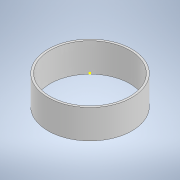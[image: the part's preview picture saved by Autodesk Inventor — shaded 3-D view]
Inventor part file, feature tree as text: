
AUTODESK INVENTOR PART (.ipt)
format: ipt  version: 2020 (Build 240168000, 168)  size: 233,472 bytes
history: native  units: in
note: dims shown in document units (in); Inventor stores cm internally (conversion verified against a paired STEP export)
features: sketch x2, extrude x1
ambient origin geometry x8: Origin, YZ Plane, XZ Plane, XY Plane, X Axis, Y Axis, Z Axis, Center Point
bodies: Solid1 (feature_tree)
feature tree (3):
  extrude  "Extrusion1"  Depth=0.7992in
  sketch  "Sketch2"  dims[d2=0.2756in d3=0.0in]
  sketch  "Sketch1"  dims[d0=0.7598in d1=0.7992in]
